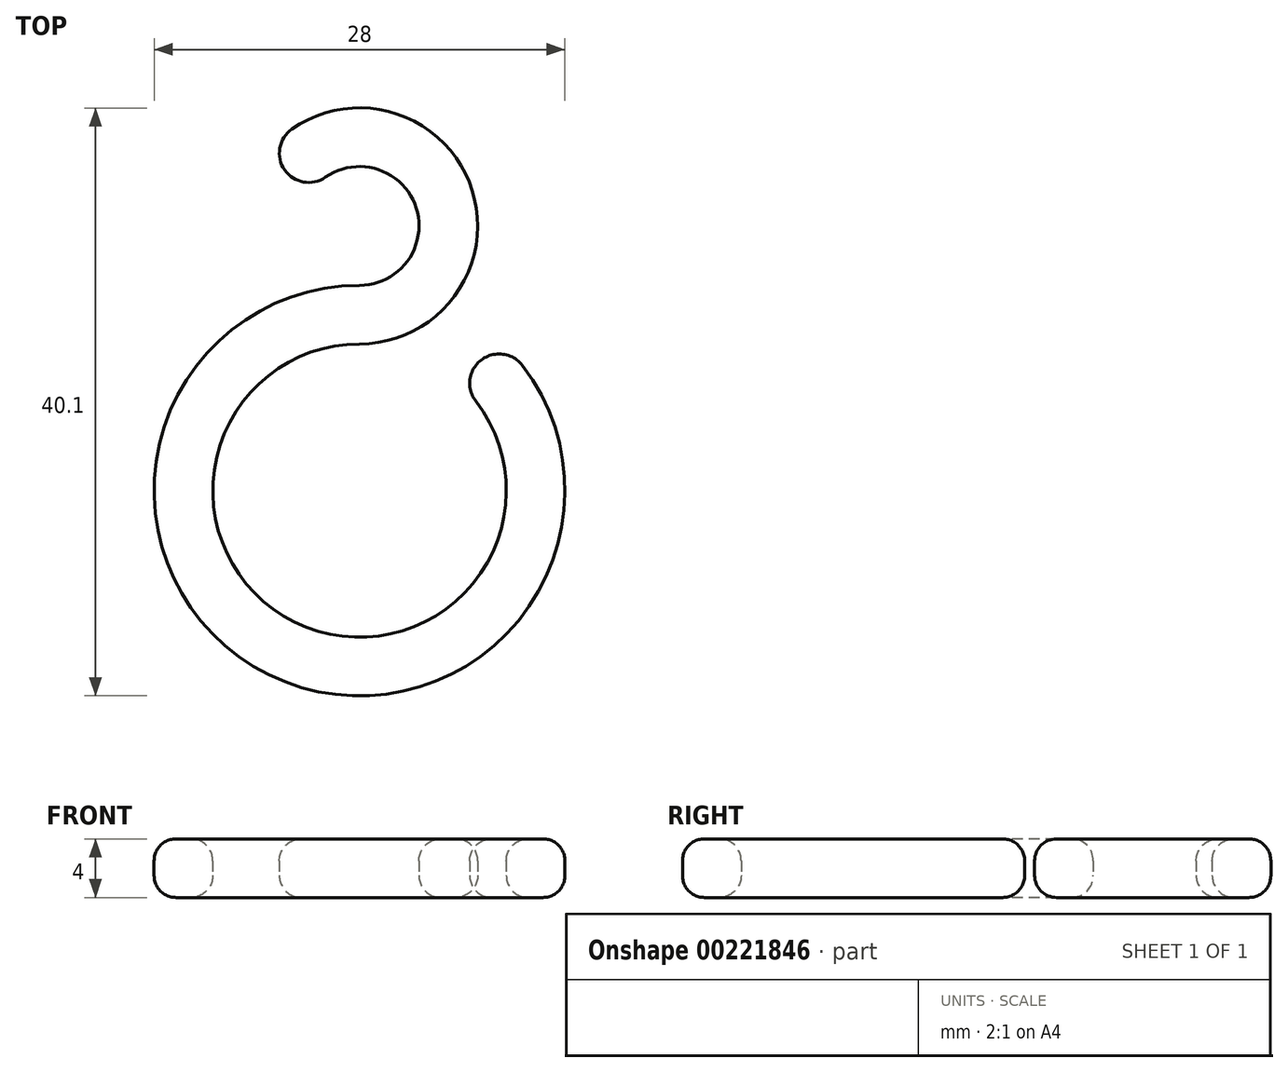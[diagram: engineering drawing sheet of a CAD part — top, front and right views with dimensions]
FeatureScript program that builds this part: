
annotation { "Feature Type Name" : "Feature", "Feature Type Description" : "" }
export const myFeature = defineFeature(function(context is Context, id is Id, definition is map)
    precondition{}
    {
        {
            var Q0;
            Q0=qCreatedBy(makeId("Top.planeOp"),FACE);
            var sketch = newSketch(context, id + "F0", { "sketchPlane" : qUnion([Q0])});
            skArc(sketch, "E0", {"start": v(-3.26, 21.15) * mm, "mid": v(0.4, 26.94) * mm, "end": v(-6.4, 27.76) * mm});
            skArc(sketch, "E1", {"start": v(-3.26, 17.15) * mm, "mid": v(-6.46, -2.32) * mm, "end": v(2.8, 15.11) * mm});
            skArc(sketch, "E2", {"start": v(-3.26, 21.15) * mm, "mid": v(-8.72, -5.74) * mm, "end": v(6.78, 16.9) * mm});
            skArc(sketch, "E3", {"start": v(-3.26, 17.15) * mm, "mid": v(3.81, 29.04) * mm, "end": v(-10.01, 29.59) * mm});
            skLineSegment(sketch, "E4", {"start": v(-6.4, 27.76) * mm, "end": v(-10.01, 29.59) * mm});
            skLineSegment(sketch, "E5", {"start": v(2.8, 15.11) * mm, "end": v(6.78, 16.9) * mm});
            skPoint(sketch, "E6.orphan", {"position": v(2.71, 19.81) * mm});
            skSolve(sketch);
        }
        {
            var Q0;
            Q0 = qSketchRegion(id + "F0", true);
            extrude(context, id + "F1", {"entities" : qUnion([Q0]), "depth" : 4 * mm});
        }
        {
            var Q0;
            Q0=makeQuery(id+"F1.opExtrude","SWEPT_EDGE",EDGE,{"disambiguationData":[OSD([sQuery(id+"F0.wireOp",EDGE,"E3"),sQuery(id+"F0.wireOp",EDGE,"E4")])]});
            var Q1;
            Q1=makeQuery(id+"F1.opExtrude","SWEPT_EDGE",EDGE,{"disambiguationData":[OSD([sQuery(id+"F0.wireOp",EDGE,"E0"),sQuery(id+"F0.wireOp",EDGE,"E4")])]});
            var Q2;
            Q2=makeQuery(id+"F1.opExtrude","SWEPT_EDGE",EDGE,{"disambiguationData":[OSD([sQuery(id+"F0.wireOp",EDGE,"E1"),sQuery(id+"F0.wireOp",EDGE,"E5")])]});
            var Q3;
            Q3=makeQuery(id+"F1.opExtrude","SWEPT_EDGE",EDGE,{"disambiguationData":[OSD([sQuery(id+"F0.wireOp",EDGE,"E2"),sQuery(id+"F0.wireOp",EDGE,"E5")])]});
            fillet(context, id + "F2", {"entities" : qUnion([Q0, Q1, Q2, Q3]), "radius" : 2 * mm, "tangentPropagation" : true, "allowEdgeOverflow" : false});
        }
        {
            var Q0;
            Q0=makeQuery(id+"F1.opExtrude","CAP_EDGE",EDGE,{"disambiguationData":[OSD([sQuery(id+"F0.wireOp",EDGE,"E2")])],"isStart":false});
            var Q1;
            Q1=makeQuery(id+"F1.opExtrude","CAP_EDGE",EDGE,{"disambiguationData":[OSD([sQuery(id+"F0.wireOp",EDGE,"E2")])],"isStart":true});
            fillet(context, id + "F3", {"entities" : qUnion([Q0, Q1]), "radius" : 1.5 * mm, "tangentPropagation" : true, "allowEdgeOverflow" : false});
        }
    });
